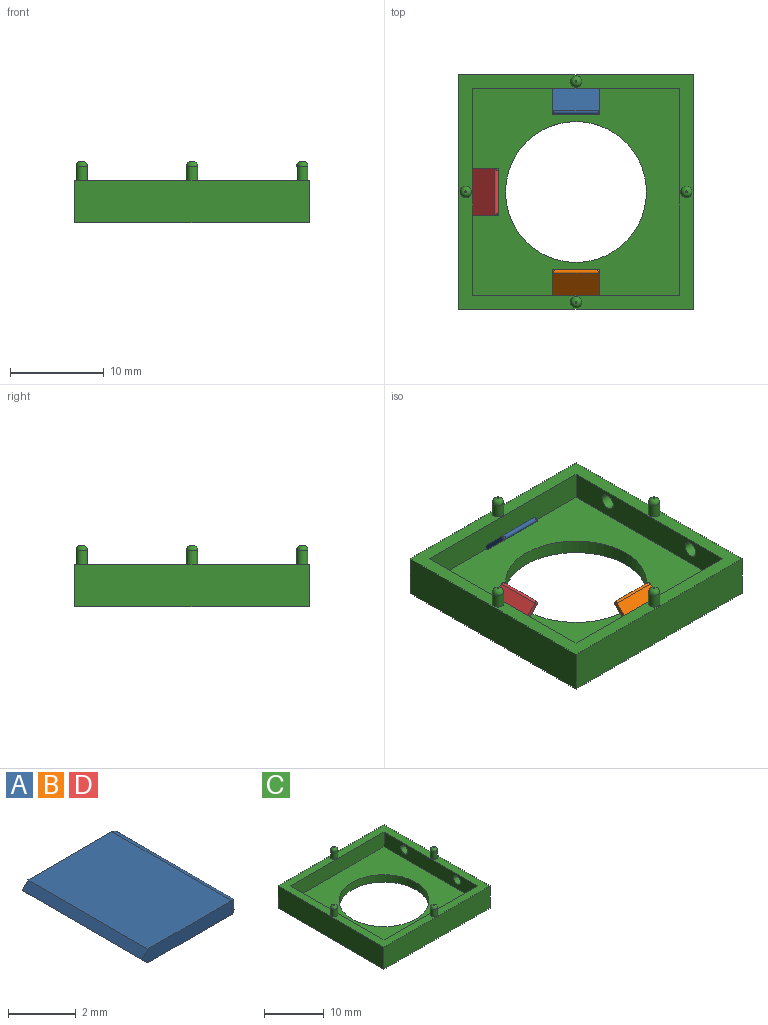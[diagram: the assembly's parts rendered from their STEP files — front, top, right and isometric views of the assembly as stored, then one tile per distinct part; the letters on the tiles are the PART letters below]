
ASSEMBLY  parts=4 mates=3
PART A: 9 faces, bbox 4x5x0.5 mm
  f0: plane 3.75x0.5mm, normal (0,-1,0), area 1.8mm2, adj f1,f3,f6,f7,f8
  f1: plane 5x3.5mm, normal (0,0,-1), area 17.5mm2, adj f0,f2,f5,f8
  f2: plane 3.75x0.5mm, normal (0,1,0), area 1.8mm2, adj f1,f3,f4,f7,f8
  f3: plane 5x3.5mm, normal (0,0,1), area 17.5mm2, adj f0,f2,f5,f7
  f4: cylinder r=0.25mm len=0.5mm, axis (0,0,1), area 0.1mm2, adj f2,f5
  f5: cylinder r=0.25mm len=5mm, axis (0,-1,0), area 3.7mm2, adj f1,f3,f4,f6
  f6: cylinder r=0.25mm len=0.5mm, axis (0,0,-1), area 0.1mm2, adj f0,f5
  f7: plane 5x0.25mm, normal (-0.71,0,0.71), area 1.8mm2, adj f0,f2,f3,f8
  f8: plane 5x0.25mm, normal (-0.71,0,-0.71), area 1.8mm2, adj f0,f1,f2,f7
PART B: same geometry as A
PART C: 26 faces, bbox 25x25x6.5 mm
  f0: plane 25x25mm, normal (0,0,1), area 136.5mm2, adj f2,f3,f4,f5,f7,f8,f9,f10
  f1: cylinder r=7.5mm len=15mm, axis (0,0,1), area 70.7mm2, adj f6,f11
  f2: plane 25x4.5mm, normal (0,-1,0), area 112.5mm2, adj f0,f3,f5,f6
  f3: plane 25x4.5mm, normal (1,0,0), area 108.3mm2, adj f0,f2,f4,f6,f24,f25
  f4: plane 25x4.5mm, normal (0,1,0), area 112.5mm2, adj f0,f3,f5,f6
  f5: plane 25x4.5mm, normal (-1,0,0), area 112.5mm2, adj f0,f2,f4,f6
  f6: plane 25x25mm, normal (0,0,-1), area 448.3mm2, adj f1,f2,f3,f4,f5
  f7: plane 22x3mm, normal (0,1,0), area 66mm2, adj f0,f8,f10,f11
  f8: plane 22x3mm, normal (-1,0,0), area 61.8mm2, adj f0,f7,f9,f11,f24,f25
  f9: plane 22x3mm, normal (0,-1,0), area 66mm2, adj f0,f8,f10,f11
  f10: plane 22x3mm, normal (1,0,0), area 66mm2, adj f0,f7,f9,f11
  f11: plane 22x22mm, normal (0,0,1), area 307.3mm2, adj f1,f7,f8,f9,f10
  f12: cylinder r=0.6mm len=1.5mm, axis (0,0,-1), area 5.7mm2, adj f0,f23
  f13: plane 0.2x0.2mm, normal (0,0,1), area 0mm2, adj f23
  f14: cylinder r=0.6mm len=1.5mm, axis (0,0,-1), area 5.7mm2, adj f0,f20
  f15: plane 0.2x0.2mm, normal (0,0,1), area 0mm2, adj f20
  f16: cylinder r=0.6mm len=1.5mm, axis (0,0,-1), area 5.7mm2, adj f0,f21
  f17: plane 0.2x0.2mm, normal (0,0,1), area 0mm2, adj f21
  f18: cylinder r=0.6mm len=1.5mm, axis (0,0,-1), area 5.7mm2, adj f0,f22
  f19: plane 0.2x0.2mm, normal (0,0,1), area 0mm2, adj f22
  f20: torus R=0.1mm, axis (0,0,1), area 2.1mm2, adj f14,f15
  f21: torus R=0.1mm, axis (0,0,1), area 2.1mm2, adj f16,f17
  f22: torus R=0.1mm, axis (0,0,1), area 2.1mm2, adj f18,f19
  f23: torus R=0.1mm, axis (0,0,1), area 2.1mm2, adj f12,f13
  f24: cylinder r=0.81mm len=1.63mm, axis (1,0,0), area 7.7mm2, adj f3,f8
  f25: cylinder r=0.81mm len=1.63mm, axis (1,0,0), area 7.7mm2, adj f3,f8
PART D: same geometry as A
PLACE A rot(axis=(-0.36,-0.36,-0.86),98.4deg) t=(-5.58,9.22,3.59)mm
PLACE B rot(axis=(0.36,-0.36,0.86),98.4deg) t=(-5.58,-10.66,3.59)mm
PLACE C t=(-5.58,-0.72,0.5)mm
PLACE D rot(axis=(0,-1,0),45deg) t=(-15.52,-0.72,3.59)mm
MATE fastened D.f8 <-> C.f11  axis (0,0,-1) through (-16.58,-0.72,2)mm
MATE fastened B.f8 <-> C.f11  axis (0,0,-1) through (-5.58,-11.72,2)mm
MATE fastened A.f8 <-> C.f11  axis (0,0,-1) through (-5.58,10.28,2)mm
